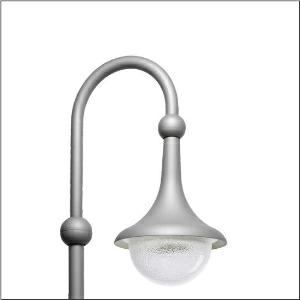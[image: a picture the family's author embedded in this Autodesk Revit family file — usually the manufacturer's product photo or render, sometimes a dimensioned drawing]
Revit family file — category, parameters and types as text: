
# Revit family: kleine_glocke___st1_2a_5xa1573e1b208_4df3
name_source: partatom
category: Lighting Fixtures
units: mm (PartAtom-declared; Revit-internal decimal feet)

## family parameters
Cut with Voids When Loaded = No
Host = Face
Light Source = No
Part Type = Normal
Room Calculation Point = No
Round Connector Dimension = Use Diameter
Shared = No

## types (1)
- --- (1 x LED, 1660 lm, 13.2 W, 3000K)
    Apparent Load = 13 VA
    CIE Flux Codes = 28 64 93 98 100
    Color Rendering = 70
    Color Temperature = 3000K
    Default Elevation = 1800 mm
    Description = Small Bell, mast luminaire, primary light control with 3 zone facetted reflector, of plastic, aluminium vaporised, primary optical cover: enclosure, of PMMA, transparent structured, light distribution: ST1.2a, light emission: direct distribution, primary light characteristic: asymmetric, installation type: suspended mounting, LED, High Power LED, rated luminous flux: 1.660lm, luminous efficacy: 126lm/W, light colour: 730, colour temperature: 3000K, control gear: ECG Plus, control: flexible luminous flux parameterisation, time-dependent luminous flux control, constant luminous flux control, digital communication interface, power reduction, electronic power reduction, mains connection: 230..240V, AC, 50/60Hz, start of lifetime: 13W, end of service life: 14W, reduction: 7W, luminaire housing, bell-shaped, of glass-fibre reinforced polyester, coated, Siteco® metallic grey (DB 702S), please order curved mast extension separately, diameter: 430mm, height: 575mm, protection rating (complete): IP54, insulation class (complete): insulation class II (safety insulation), certification: CE, ENEC, VDE, impact resistance: IK07, standard-compliant lighting for roads and squares, packaging unit: 1 piece

Light Distribution: ST1.2a
    Height = 575 mm
    Lamp = 1 x LED
    Lamp Light Flux = 1660 lm
    Lamp Power = 13.2 W
    Lamp count = 1
    Length = 430 mm
    Luminous efficacy = 126 lm/W
    Manufacturer = Siteco
    ModVariant = No
    Model = 5XA1573E1B208
    Number of Poles = 1
    OnlyDefault = Yes
    Power Factor = 1
    Product Name = Kleine Glocke | ST1.2a
    Product group = mast luminaire | pylon annexe
    ProductGroupID = 6201
    Protection Class = Protection class II
    Protection Degree = IP 54
    RLX_Detail_Level = 1
    RLX_Emergency_Light_Flux = 0 lm
    RLX_Emergency_Type = 0
    RLX_Emergency_Type_DB = No
    RlxData = <blob elided: 51789 chars, md5=035da553>
    Socket = socket
    Standby Power = 0 W
    System Light Flux = 1660 lm
    System Power = 13 W
    Type Comments = factory setting: luminous flux: 100 % | dim-lin: 254 | 249 mA
    Type Image = l_1284392.jpg
    URL = http://relux.com
    VarID = @adj_129359
    Voltage = 0 V
    Weight = 0.00 kg
    Width = 0 mm  [stored 0 ft]

note: [stored X ft] marks values corroborated as IEEE doubles in the binary element streams (Revit-internal decimal feet)

## geometry (parser evidence)
native form markers: Blend x4, Sweep x12
no freeform markers — native parametric forms only
